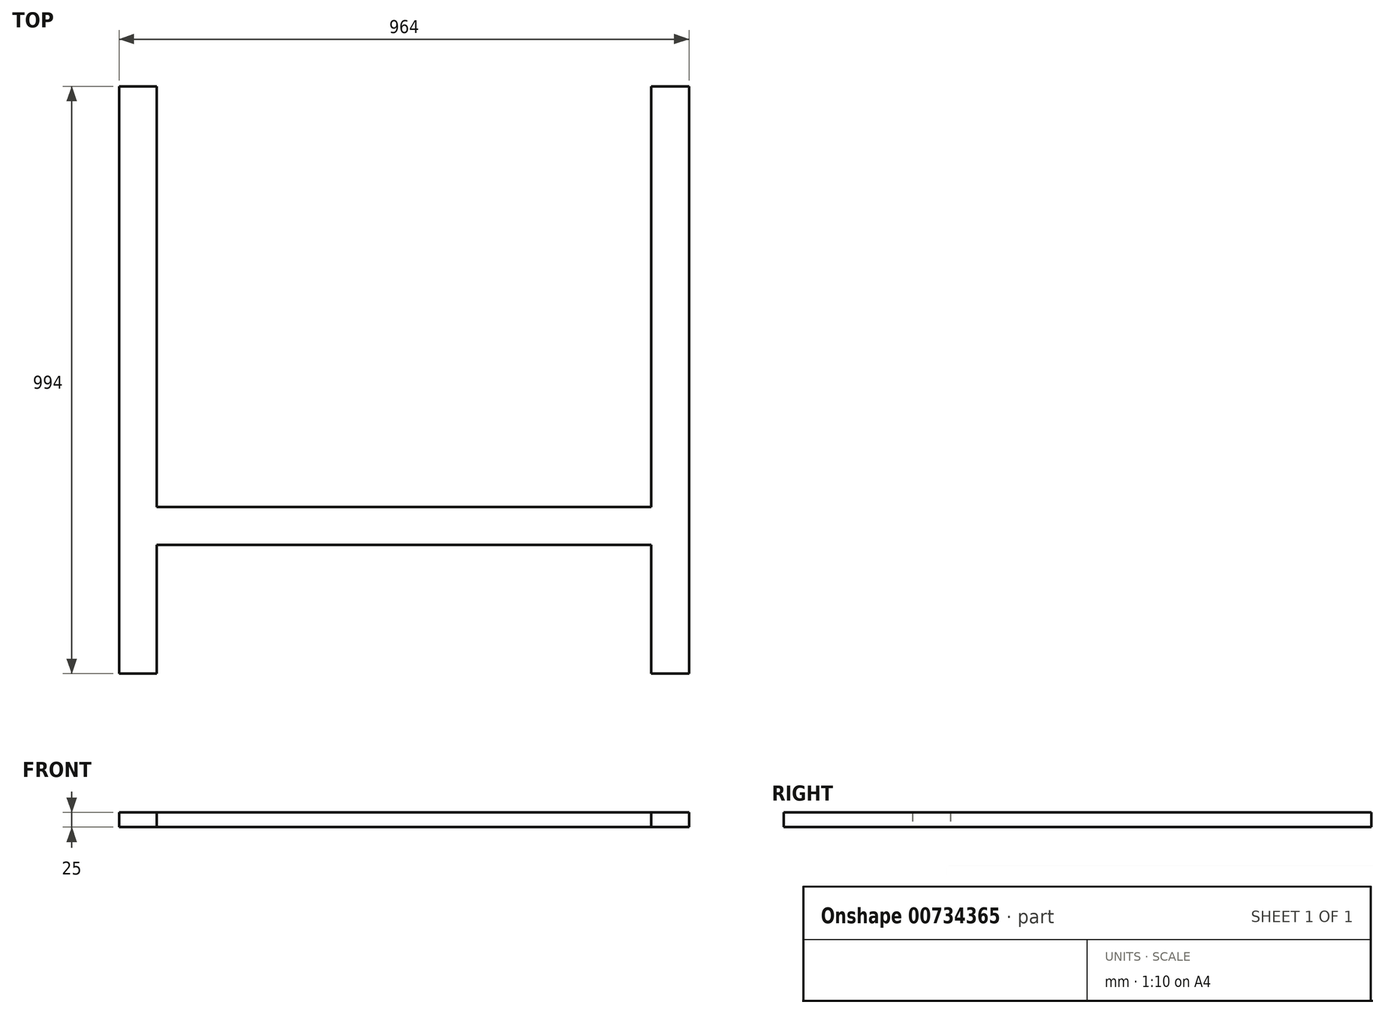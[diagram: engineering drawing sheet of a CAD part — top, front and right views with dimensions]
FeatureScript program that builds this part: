
annotation { "Feature Type Name" : "Feature", "Feature Type Description" : "" }
export const myFeature = defineFeature(function(context is Context, id is Id, definition is map)
    precondition{}
    {
        {
            var Q0;
            Q0=qCreatedBy(makeId("Top.planeOp"),FACE);
            var sketch = newSketch(context, id + "F0", { "sketchPlane" : qUnion([Q0])});
            skLineSegment(sketch, "E0.bottom", {"start": v(-418, 32) * mm, "end": v(418, 32) * mm});
            skLineSegment(sketch, "E0.top", {"start": v(-418, -32) * mm, "end": v(418, -32) * mm});
            skPoint(sketch, "E0.middle", {"position": v(0, 0) * mm});
            skLineSegment(sketch, "E1", {"start": v(-418, 32) * mm, "end": v(-418, 744) * mm});
            skLineSegment(sketch, "E2", {"start": v(-418, 744) * mm, "end": v(-482, 744) * mm});
            skLineSegment(sketch, "E3", {"start": v(-482, 744) * mm, "end": v(-482, -250) * mm});
            skLineSegment(sketch, "E4", {"start": v(-482, -250) * mm, "end": v(-418, -250) * mm});
            skLineSegment(sketch, "E5", {"start": v(-418, -250) * mm, "end": v(-418, -32) * mm});
            skLineSegment(sketch, "E6", {"start": v(418, 32) * mm, "end": v(418, 744) * mm});
            skLineSegment(sketch, "E7", {"start": v(418, 744) * mm, "end": v(482, 744) * mm});
            skLineSegment(sketch, "E8", {"start": v(482, 744) * mm, "end": v(482, -250) * mm});
            skLineSegment(sketch, "E9", {"start": v(482, -250) * mm, "end": v(418, -250) * mm});
            skLineSegment(sketch, "E10", {"start": v(418, -250) * mm, "end": v(418, -32) * mm});
            skSolve(sketch);
        }
        {
            var Q0;
            Q0 = qSketchRegion(id + "F0", true);
            extrude(context, id + "F1", {"entities" : qUnion([Q0]), "depth" : 25 * mm, "offsetDistance" : 25 * mm});
        }
    });
